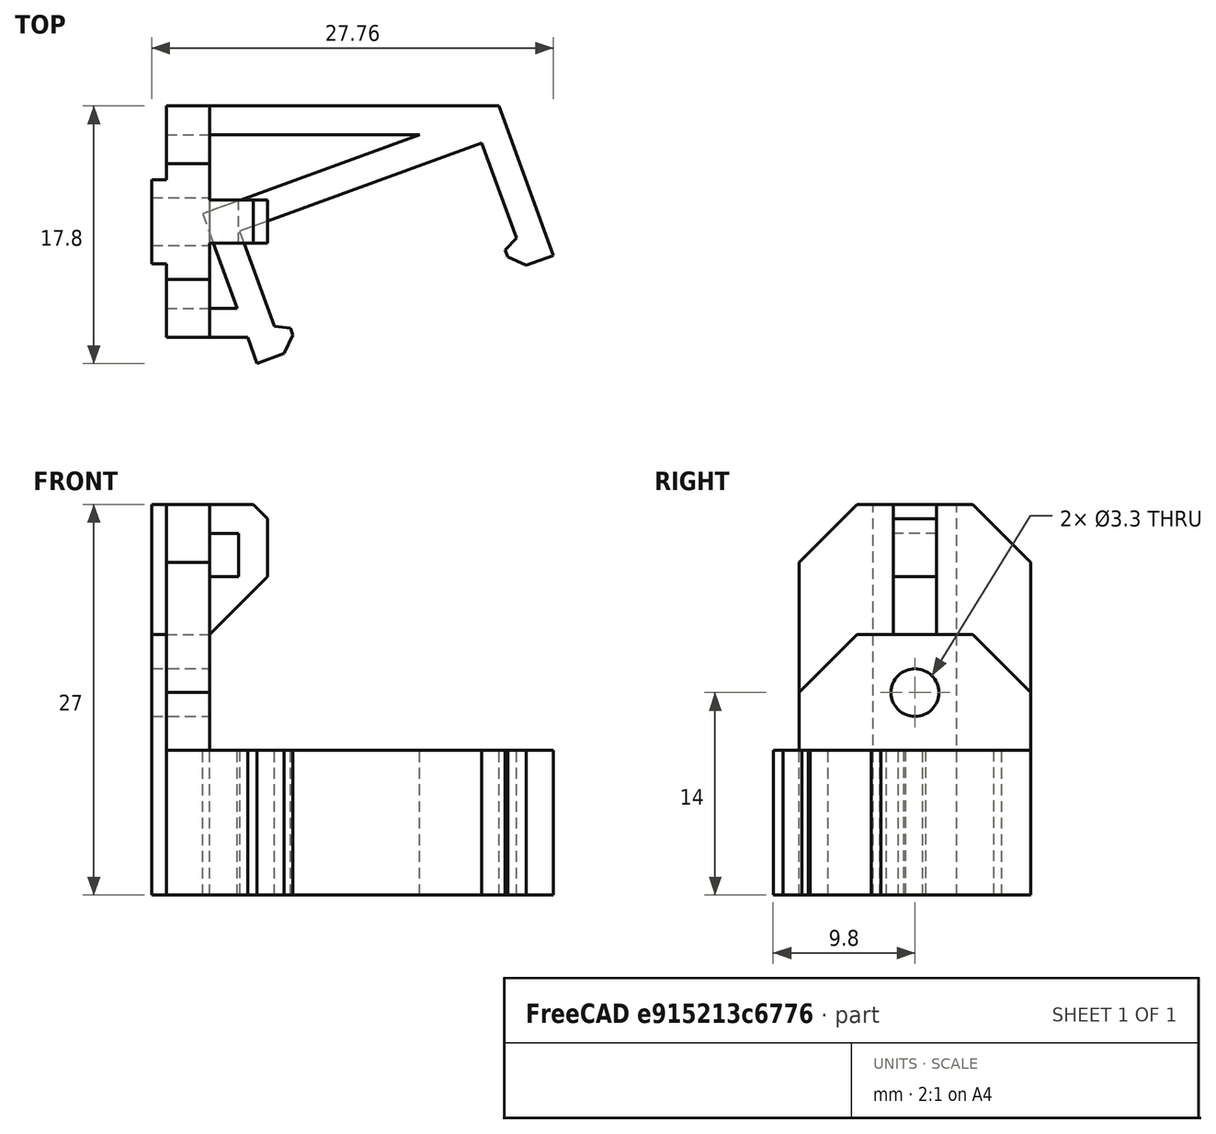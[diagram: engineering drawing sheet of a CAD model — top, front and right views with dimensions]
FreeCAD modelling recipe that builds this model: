
FCSTD DOCUMENT  (FreeCAD 0.19R24291 (Git))
Label: led-mount
License: All rights reserved
LicenseURL: http://en.wikipedia.org/wiki/All_rights_reserved
objects: Part::Box×8, Part::MultiFuse×6, Part::Chamfer×4, Part::Feature×3, Part::Cut×3, Part::Cylinder×2, Part::Refine×1
note: 27 computed .brp shape members not serialized (recipe doc carries the construction recipe); baked Part::Feature solids carry a one-line shape summary decoded from their .brp

FEATURE [Part::Feature] Fusion038001001001001  label="arm"
  Placement = pos=(0,0,0) rot=(0,0,1;3.49066rad)
  shape: bbox 24.25 x 17.79 x 10 mm, 16 faces (baked)
FEATURE [Part::Refine] Fusion038001001001001001  label="arm001"
  Placement = pos=(23,18,0) rot=(0,0,1;0rad)
  Source = -> Fusion038001001001001
FEATURE [Part::Box] Box  label="Cube"
  AttacherType = Attacher::AttachEngine3D
  Height = 27
  Length = 3
  Placement = pos=(0,2,0) rot=(0,0,1;0rad)
  Width = 16
FEATURE [Part::Box] Box001  label="Cube001"
  AttacherType = Attacher::AttachEngine3D
  Height = 10
  Length = 6
  Placement = pos=(0,2,0) rot=(0,0,1;0rad)
  Width = 2
FEATURE [Part::Box] Box002  label="Cube002"
  AttacherType = Attacher::AttachEngine3D
  Height = 10
  Length = 23
  Placement = pos=(0,16,0) rot=(0,0,1;0rad)
  Width = 2
FEATURE [Part::MultiFuse] Fusion  label="arm-base"
  Shapes = -> [Box001,Fusion038001001001001001,Box002]
FEATURE [Part::Box] Box003  label="Cube003"
  AttacherType = Attacher::AttachEngine3D
  Height = 18
  Length = 3
  Placement = pos=(0,2,0) rot=(0,0,1;0rad)
  Width = 16
FEATURE [Part::Cylinder] Cylinder
  Angle = 360
  AttacherType = Attacher::AttachEngine3D
  Height = 10
  Placement = pos=(-4,10,14) rot=(0,1,0;1.5708rad)
  Radius = 1.65
FEATURE [Part::Chamfer] Chamfer
  Base = -> Box003
  Edges = 2 edges r=4: [Edge10,Edge12]
FEATURE [Part::Box] Box004  label="Cube004"
  AttacherType = Attacher::AttachEngine3D
  Height = 27
  Length = 2
  Placement = pos=(-1,7.1,0) rot=(0,0,1;0rad)
  Width = 5.8
FEATURE [Part::Box] Box005  label="Cube005"
  AttacherType = Attacher::AttachEngine3D
  Height = 18
  Length = 2
  Placement = pos=(-1,7.1,0) rot=(0,0,1;0rad)
  Width = 5.8
FEATURE [Part::MultiFuse] Fusion038001001001001002
  Shapes = -> [Box005,Chamfer]
FEATURE [Part::Cut] Cut
  Base = -> Fusion038001001001001002
  Tool = -> Cylinder
FEATURE [Part::Feature] Fusion038001001001001003  label="arm-base001"
  shape: bbox 26.76 x 17.8 x 10 mm, 32 faces (baked)
FEATURE [Part::MultiFuse] Fusion038001001001001004  label="simple-mount"
  Shapes = -> [Cut,Fusion038001001001001003]
FEATURE [Part::Feature] Fusion038001001001001005  label="arm-base002"
  shape: bbox 26.76 x 17.8 x 10 mm, 32 faces (baked)
FEATURE [Part::Cylinder] Cylinder001
  Angle = 360
  AttacherType = Attacher::AttachEngine3D
  Height = 10
  Placement = pos=(-4,10,14) rot=(0,1,0;1.5708rad)
  Radius = 1.65
FEATURE [Part::Box] Box006  label="Cube006"
  AttacherType = Attacher::AttachEngine3D
  Height = 3
  Length = 3
  Placement = pos=(2,8.5,22) rot=(0,0,1;0rad)
  Width = 3
FEATURE [Part::Box] Box007  label="Cube007"
  AttacherType = Attacher::AttachEngine3D
  Height = 9
  Length = 5
  Placement = pos=(2,8.5,18) rot=(0,0,1;0rad)
  Width = 3
FEATURE [Part::Chamfer] Chamfer001
  Base = -> Box007
  Edges = 1 edges r=4: [Edge8]
FEATURE [Part::Cut] Cut001
  Base = -> Chamfer001
  Tool = -> Box006
FEATURE [Part::Chamfer] Chamfer002
  Base = -> Cut001
  Edges = 1 edges r=1: [Edge4]
FEATURE [Part::Chamfer] Chamfer003
  Base = -> Box
  Edges = 2 edges r=4: [Edge10,Edge12]
FEATURE [Part::MultiFuse] Fusion038001001001001006
  Shapes = -> [Chamfer003,Chamfer002]
FEATURE [Part::MultiFuse] Fusion038001001001001007
  Shapes = -> [Fusion038001001001001006,Box004]
FEATURE [Part::Cut] Cut002
  Base = -> Fusion038001001001001007
  Tool = -> Cylinder001
FEATURE [Part::MultiFuse] Fusion038001001001001008  label="w-wire-mounter"
  Shapes = -> [Cut002,Fusion038001001001001005]
